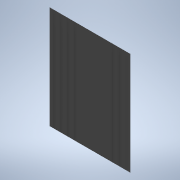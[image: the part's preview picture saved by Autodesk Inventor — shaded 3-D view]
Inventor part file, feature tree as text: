
AUTODESK INVENTOR PART (.ipt)
format: ipt  version: 2021 (Build 250183000, 183)  size: 510,464 bytes
history: native  units: in
note: dims shown in document units (in); Inventor stores cm internally (conversion verified against a paired STEP export)
features: extrude x1, pattern_linear x1, sketch x1
ambient origin geometry x8: Origin, YZ Plane, XZ Plane, XY Plane, X Axis, Y Axis, Z Axis, Center Point
bodies: Solid1 (feature_tree)
feature tree (3):
  extrude  "Extrusion1"  Depth=3.0in
  pattern_linear  "Rectangular Pattern1"  Spacing1=0.0006in  [1 undecoded]
  sketch  "Sketch1"  dims[d0=0.0098in d1=3.0in d2=0.0006in d3=0.0in d4=59.0551in d6=0.0157in]
note: 1 required parameter value undecoded (feature->parameter linkage not recoverable at this tier; creation-order binding heuristic only, values carry confidence <= 0.55)
